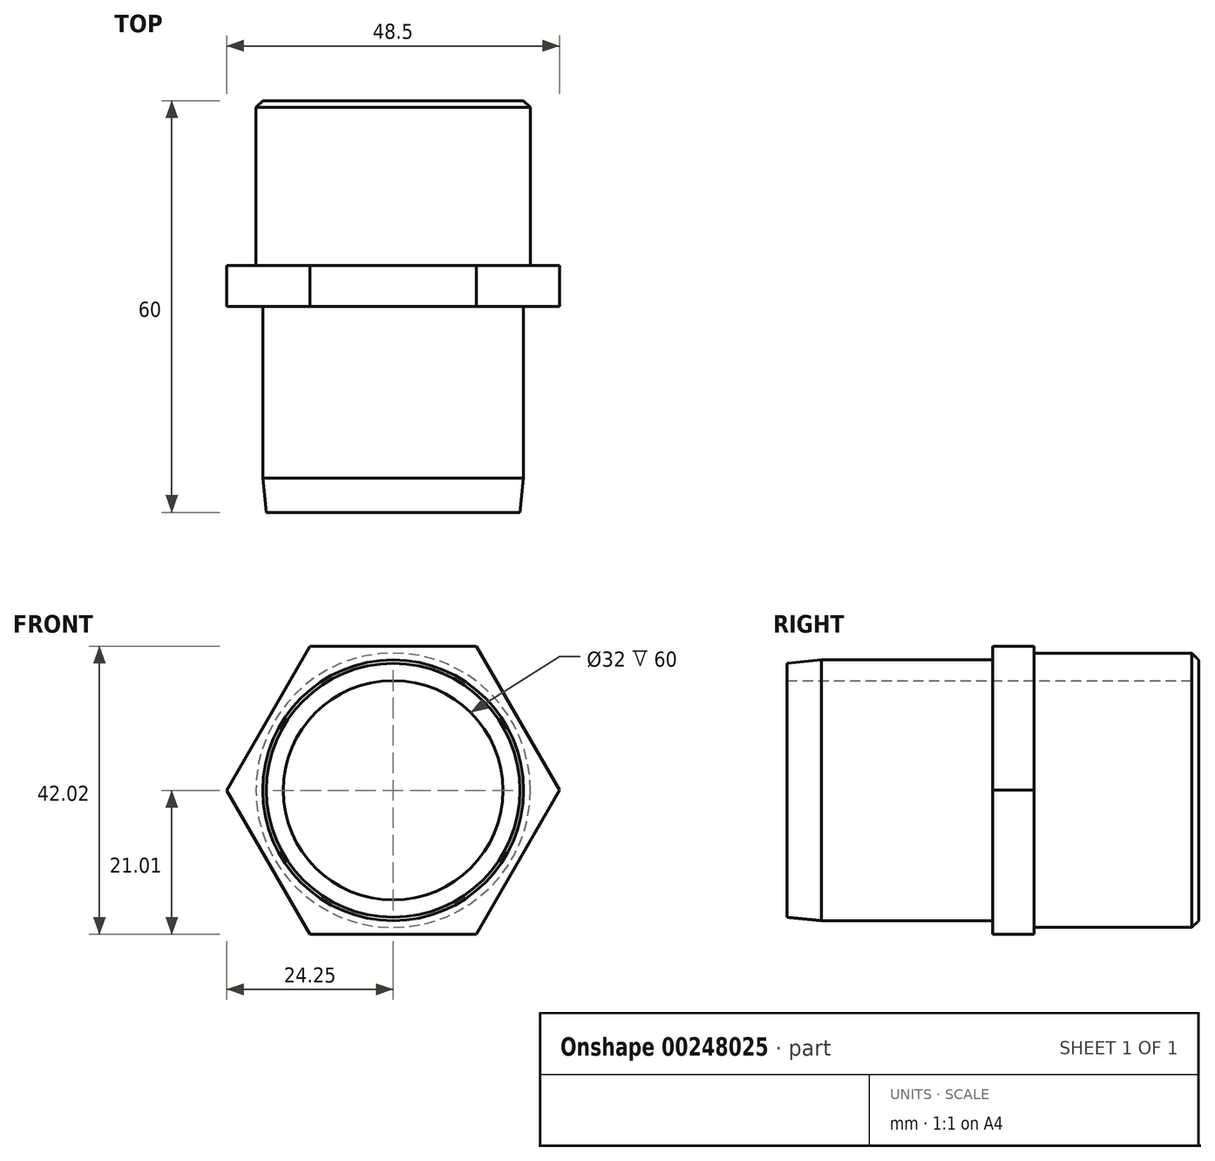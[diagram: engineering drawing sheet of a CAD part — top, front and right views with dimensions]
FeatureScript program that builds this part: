
annotation { "Feature Type Name" : "Feature", "Feature Type Description" : "" }
export const myFeature = defineFeature(function(context is Context, id is Id, definition is map)
    precondition{}
    {
        {
            var Q0;
            Q0=qCreatedBy(makeId("Front.planeOp"),FACE);
            var sketch = newSketch(context, id + "F0", { "sketchPlane" : qUnion([Q0])});
            skLineSegment(sketch, "E0.0", {"start": v(12.1, 21.01) * mm, "end": v(24.25, 0.03) * mm});
            skLineSegment(sketch, "E0.1", {"start": v(24.25, 0.03) * mm, "end": v(12.15, -20.99) * mm});
            skLineSegment(sketch, "E0.2", {"start": v(12.15, -20.99) * mm, "end": v(-12.1, -21.01) * mm});
            skLineSegment(sketch, "E0.3", {"start": v(-12.1, -21.01) * mm, "end": v(-24.25, -0.03) * mm});
            skLineSegment(sketch, "E0.4", {"start": v(-24.25, -0.03) * mm, "end": v(-12.15, 20.99) * mm});
            skLineSegment(sketch, "E0.5", {"start": v(-12.15, 20.99) * mm, "end": v(12.1, 21.01) * mm});
            skPoint(sketch, "E0.0.midPoint", {"position": v(18.18, 10.52) * mm});
            skSolve(sketch);
        }
        {
            var Q0;
            Q0=makeQuery(id+"F0.imprint","IMPRINT",FACE,{"disambiguationData":[TD([[makeQuery(id+"F0.imprint","IMPRINT",EDGE,{"derivedFrom":sQuery(id+"F0.wireOp",EDGE,"E0.0")}),-1.0]])]});
            extrude(context, id + "F1", {"entities" : qUnion([Q0]), "depth" : 6 * mm, "offsetDistance" : 25 * mm});
        }
        {
            var Q0;
            Q0=makeQuery(id+"F1.opExtrude","CAP_FACE",FACE,{"disambiguationData":[OSD([sQuery(id+"F0.wireOp",EDGE,"E0.0"),sQuery(id+"F0.wireOp",EDGE,"E0.1"),sQuery(id+"F0.wireOp",EDGE,"E0.2"),sQuery(id+"F0.wireOp",EDGE,"E0.3"),sQuery(id+"F0.wireOp",EDGE,"E0.4"),sQuery(id+"F0.wireOp",EDGE,"E0.5")])],"isStart":false});
            var sketch = newSketch(context, id + "F2", { "sketchPlane" : qUnion([Q0])});
            skCircle(sketch, "E1", {"center": v(0, 0) * mm, "radius": 19 * mm});
            skSolve(sketch);
        }
        {
            var Q0;
            Q0=makeQuery(id+"F2.imprint","IMPRINT",FACE,{"disambiguationData":[TD([[makeQuery(id+"F2.imprint","IMPRINT",EDGE,{"derivedFrom":sQuery(id+"F2.wireOp",EDGE,"E1")}),1.0]])]});
            extrude(context, id + "F3", {"entities" : qUnion([Q0]), "operationType" : NewBodyOperationType.ADD, "depth" : 30 * mm, "offsetDistance" : 25 * mm});
        }
        {
            var Q0;
            Q0=makeQuery(id+"F1.opExtrude","CAP_FACE",FACE,{"disambiguationData":[OSD([sQuery(id+"F0.wireOp",EDGE,"E0.0"),sQuery(id+"F0.wireOp",EDGE,"E0.1"),sQuery(id+"F0.wireOp",EDGE,"E0.2"),sQuery(id+"F0.wireOp",EDGE,"E0.3"),sQuery(id+"F0.wireOp",EDGE,"E0.4"),sQuery(id+"F0.wireOp",EDGE,"E0.5")])],"isStart":true});
            var sketch = newSketch(context, id + "F4", { "sketchPlane" : qUnion([Q0])});
            skCircle(sketch, "E2", {"center": v(0, 0) * mm, "radius": 20 * mm});
            skSolve(sketch);
        }
        {
            var Q0;
            Q0=makeQuery(id+"F4.imprint","IMPRINT",FACE,{"disambiguationData":[TD([[makeQuery(id+"F4.imprint","IMPRINT",EDGE,{"derivedFrom":sQuery(id+"F4.wireOp",EDGE,"E2")}),1.0]])]});
            extrude(context, id + "F5", {"entities" : qUnion([Q0]), "operationType" : NewBodyOperationType.ADD, "depth" : 24 * mm, "offsetDistance" : 25 * mm});
        }
        {
            var Q0;
            Q0=makeQuery(id+"F5.opExtrude","CAP_FACE",FACE,{"disambiguationData":[OSD([sQuery(id+"F4.wireOp",EDGE,"E2")])],"isStart":false});
            var sketch = newSketch(context, id + "F6", { "sketchPlane" : qUnion([Q0])});
            skCircle(sketch, "E3", {"center": v(0, 0) * mm, "radius": 16 * mm});
            skSolve(sketch);
        }
        {
            var Q0;
            Q0=makeQuery(id+"F6.imprint","IMPRINT",FACE,{"disambiguationData":[TD([[makeQuery(id+"F6.imprint","IMPRINT",EDGE,{"derivedFrom":sQuery(id+"F6.wireOp",EDGE,"E3")}),1.0]])]});
            extrude(context, id + "F7", {"entities" : qUnion([Q0]), "operationType" : NewBodyOperationType.REMOVE, "endBound" : BoundingType.THROUGH_ALL, "oppositeDirection" : true, "depth" : 25 * mm, "offsetDistance" : 25 * mm});
        }
        {
            var Q0;
            Q0=makeQuery(id+"F5.opExtrude","CAP_EDGE",EDGE,{"disambiguationData":[OSD([sQuery(id+"F4.wireOp",EDGE,"E2")])],"isStart":false});
            chamfer(context, id + "F8", {"entities" : qUnion([Q0]), "width" : 1 * mm, "tangentPropagation" : true});
        }
        {
            var Q0;
            Q0=makeQuery(id+"F3.opExtrude","CAP_EDGE",EDGE,{"disambiguationData":[OSD([sQuery(id+"F2.wireOp",EDGE,"E1")])],"isStart":false});
            chamfer(context, id + "F9", {"entities" : qUnion([Q0]), "chamferType" : ChamferType.TWO_OFFSETS, "width1" : 0.5 * mm, "oppositeDirection" : false, "width2" : 5 * mm, "tangentPropagation" : true});
        }
    });
